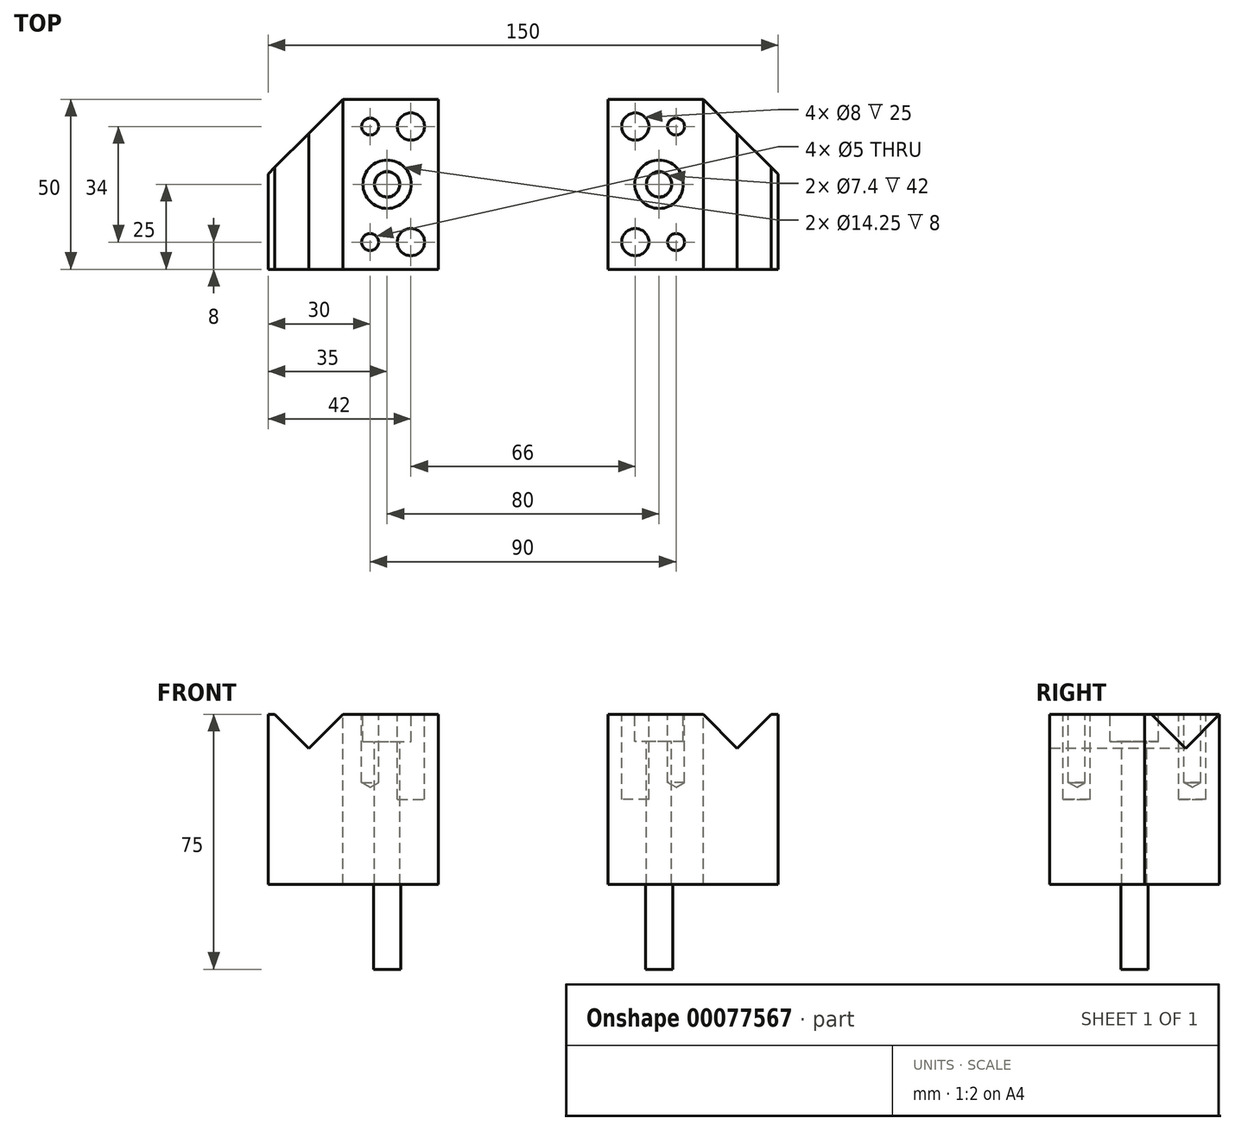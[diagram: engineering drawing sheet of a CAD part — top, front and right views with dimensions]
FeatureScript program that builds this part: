
annotation { "Feature Type Name" : "Feature", "Feature Type Description" : "" }
export const myFeature = defineFeature(function(context is Context, id is Id, definition is map)
    precondition{}
    {
        {
            var Q0;
            Q0=qCreatedBy(makeId("Top.planeOp"),FACE);
            var sketch = newSketch(context, id + "F0", { "sketchPlane" : qUnion([Q0])});
            skLineSegment(sketch, "E0.bottom", {"start": v(25, 25) * mm, "end": v(-25, 25) * mm});
            skLineSegment(sketch, "E0.top", {"start": v(25, -25) * mm, "end": v(-25, -25) * mm});
            skLineSegment(sketch, "E0.left", {"start": v(25, 25) * mm, "end": v(25, -25) * mm});
            skLineSegment(sketch, "E0.right", {"start": v(-25, 25) * mm, "end": v(-25, -25) * mm});
            skPoint(sketch, "E0.middle", {"position": v(0, 0) * mm});
            skSolve(sketch);
        }
        {
            var Q0;
            Q0 = qSketchRegion(id + "F0", true);
            var Q1;
            Q1 = qSketchRegion(id + "F2", true);
            extrude(context, id + "F1", {"entities" : qUnion([Q0, Q1]), "depth" : 50 * mm});
        }
        {
            var Q0;
            Q0=makeQuery(id+"F1.opExtrude","SWEPT_FACE",FACE,{"disambiguationData":[OSD([sQuery(id+"F0.wireOp",EDGE,"E0.top")])]});
            var sketch = newSketch(context, id + "F2", { "sketchPlane" : qUnion([Q0])});
            skLineSegment(sketch, "E1", {"start": v(23, 50) * mm, "end": v(13, 40) * mm});
            skLineSegment(sketch, "E2", {"start": v(13, 40) * mm, "end": v(3, 50) * mm});
            skLineSegment(sketch, "E3", {"start": v(3, 50) * mm, "end": v(23, 50) * mm});
            skSolve(sketch);
        }
        {
            var Q0;
            Q0=makeQuery(id+"F2.imprint","IMPRINT",FACE,{"disambiguationData":[TD([[makeQuery(id+"F2.imprint","IMPRINT",EDGE,{"derivedFrom":sQuery(id+"F2.wireOp",EDGE,"E1")}),-1.0]])]});
            extrude(context, id + "F3", {"entities" : qUnion([Q0]), "operationType" : NewBodyOperationType.REMOVE, "endBound" : BoundingType.THROUGH_ALL, "oppositeDirection" : true, "depth" : 25 * mm});
        }
        {
            var Q0;
            {var subQ0=sQuery(id+"F0.wireOp",EDGE,"E0.bottom");var subQ1=sQuery(id+"F0.wireOp",EDGE,"E0.top");var subQ2=sQuery(id+"F0.wireOp",EDGE,"E0.right");Q0=makeQuery(id+"F3.boolean.opBoolean","SPLIT",FACE,{"disambiguationData":[TD([makeQuery(id+"F1.opExtrude","SWEPT_FACE",FACE,{"disambiguationData":[OSD([subQ2])]})])],"derivedFrom":makeQuery(id+"F1.opExtrude","CAP_FACE",FACE,{"disambiguationData":[OSD([subQ0,subQ1,sQuery(id+"F0.wireOp",EDGE,"E0.left"),subQ2])],"isStart":false})});}
            var sketch = newSketch(context, id + "F4", { "sketchPlane" : qUnion([Q0])});
            skCircle(sketch, "E4", {"center": v(-17, 17) * mm, "radius": 4 * mm});
            skCircle(sketch, "E5", {"center": v(-17, -17) * mm, "radius": 4 * mm});
            skSolve(sketch);
        }
        {
            var Q0;
            Q0 = qSketchRegion(id + "F4", true);
            extrude(context, id + "F5", {"entities" : qUnion([Q0]), "operationType" : NewBodyOperationType.REMOVE, "oppositeDirection" : true, "depth" : 25 * mm});
        }
        {
            var Q0;
            {var subQ0=sQuery(id+"F0.wireOp",EDGE,"E0.bottom");var subQ1=sQuery(id+"F0.wireOp",EDGE,"E0.top");var subQ2=sQuery(id+"F0.wireOp",EDGE,"E0.right");Q0=makeQuery(id+"F3.boolean.opBoolean","SPLIT",FACE,{"disambiguationData":[TD([makeQuery(id+"F1.opExtrude","SWEPT_FACE",FACE,{"disambiguationData":[OSD([subQ2])]})])],"derivedFrom":makeQuery(id+"F1.opExtrude","CAP_FACE",FACE,{"disambiguationData":[OSD([subQ0,subQ1,sQuery(id+"F0.wireOp",EDGE,"E0.left"),subQ2])],"isStart":false})});}
            var sketch = newSketch(context, id + "F6", { "sketchPlane" : qUnion([Q0])});
            skPoint(sketch, "E6", {"position": v(-15, 0) * mm});
            skPoint(sketch, "E7", {"position": v(-5, -17) * mm});
            skPoint(sketch, "E8", {"position": v(-10, 0) * mm});
            skLineSegment(sketch, "E9", {"start": v(-17, 17) * mm, "end": v(-17, -17) * mm});
            skLineSegment(sketch, "E10", {"start": v(-5, -17) * mm, "end": v(-5, 17) * mm});
            skPoint(sketch, "E11", {"position": v(-5, 17) * mm});
            skSolve(sketch);
        }
        {
            var Q0;
            Q0=sQuery(id+"F6.wireOp",VERTEX,"E7");
            var Q1;
            Q1=sQuery(id+"F6.wireOp",VERTEX,"E11");
            var Q2;
            Q2=makeQuery(id+"F1.opExtrude","SWEPT_BODY",BODY,{"disambiguationData":[OSD([sQuery(id+"F0.wireOp",EDGE,"E0.bottom"),sQuery(id+"F0.wireOp",EDGE,"E0.top"),sQuery(id+"F0.wireOp",EDGE,"E0.left"),sQuery(id+"F0.wireOp",EDGE,"E0.right")])]});
            hole(context, id + "F7", {"style" : HoleStyle.SIMPLE, "endStyle" : HoleEndStyle.BLIND, "standardTappedOrClearance" : lookupTablePath({ "standard" : "ISO", "engagement" : "75%", "pitch" : "1 mm", "size" : "M6", "type" : "Tapped" }), "standardBlindInLast" : lookupTablePath({ "standard" : "ISO", "engagement" : "75%", "pitch" : "1 mm", "size" : "M6", "type" : "Tapped" }), "holeDiameter" : 5 * mm, "holeDepth" : 20 * mm, "startFromSketch" : true, "locations" : qUnion([Q0, Q1]), "scope" : qUnion([Q2]), "majorDiameter" : 6 * mm});
        }
        {
            var Q0;
            Q0=sQuery(id+"F6.wireOp",VERTEX,"E8");
            var Q1;
            Q1=makeQuery(id+"F1.opExtrude","SWEPT_BODY",BODY,{"disambiguationData":[OSD([sQuery(id+"F0.wireOp",EDGE,"E0.bottom"),sQuery(id+"F0.wireOp",EDGE,"E0.top"),sQuery(id+"F0.wireOp",EDGE,"E0.left"),sQuery(id+"F0.wireOp",EDGE,"E0.right")])]});
            hole(context, id + "F8", {"style" : HoleStyle.C_BORE, "endStyle" : HoleEndStyle.BLIND, "standardTappedOrClearance" : lookupTablePath({ "standard" : "ISO", "engagement" : "25%", "pitch" : "1 mm", "size" : "M8", "type" : "Tapped" }), "standardBlindInLast" : lookupTablePath({ "standard" : "ISO", "engagement" : "25%", "pitch" : "1 mm", "size" : "M8", "type" : "Tapped" }), "holeDiameter" : 7.4 * mm, "cBoreDiameter" : 14.25 * mm, "cBoreDepth" : 8 * mm, "holeDepth" : 60 * mm, "startFromSketch" : true, "locations" : qUnion([Q0]), "scope" : qUnion([Q1])});
        }
        {
            var Q0;
            Q0=makeQuery(id+"F1.opExtrude","CAP_FACE",FACE,{"disambiguationData":[OSD([sQuery(id+"F0.wireOp",EDGE,"E0.bottom"),sQuery(id+"F0.wireOp",EDGE,"E0.top"),sQuery(id+"F0.wireOp",EDGE,"E0.left"),sQuery(id+"F0.wireOp",EDGE,"E0.right")])],"isStart":true});
            var sketch = newSketch(context, id + "F9", { "sketchPlane" : qUnion([Q0])});
            skCircle(sketch, "E12", {"center": v(-10, 0) * mm, "radius": 4 * mm});
            skSolve(sketch);
        }
        {
            var Q0;
            Q0 = qSketchRegion(id + "F9", true);
            extrude(context, id + "F10", {"entities" : qUnion([Q0]), "operationType" : NewBodyOperationType.ADD, "depth" : 25 * mm});
        }
        {
            var Q0;
            {var subQ0=sQuery(id+"F0.wireOp",EDGE,"E0.bottom");var subQ1=sQuery(id+"F0.wireOp",EDGE,"E0.top");var subQ2=sQuery(id+"F0.wireOp",EDGE,"E0.right");Q0=makeQuery(id+"F3.boolean.opBoolean","SPLIT",FACE,{"disambiguationData":[TD([makeQuery(id+"F1.opExtrude","SWEPT_FACE",FACE,{"disambiguationData":[OSD([subQ2])]})])],"derivedFrom":makeQuery(id+"F1.opExtrude","CAP_FACE",FACE,{"disambiguationData":[OSD([subQ0,subQ1,sQuery(id+"F0.wireOp",EDGE,"E0.left"),subQ2])],"isStart":false})});}
            var sketch = newSketch(context, id + "F11", { "sketchPlane" : qUnion([Q0])});
            skLineSegment(sketch, "E13", {"start": v(3, 25) * mm, "end": v(28, 0) * mm});
            skLineSegment(sketch, "E14", {"start": v(28, 0) * mm, "end": v(28, 25) * mm});
            skLineSegment(sketch, "E15", {"start": v(28, 25) * mm, "end": v(3, 25) * mm});
            skSolve(sketch);
        }
        {
            var Q0;
            Q0 = qSketchRegion(id + "F11", true);
            extrude(context, id + "F12", {"entities" : qUnion([Q0]), "operationType" : NewBodyOperationType.REMOVE, "endBound" : BoundingType.THROUGH_ALL, "oppositeDirection" : true, "depth" : 25 * mm});
        }
        {
            var Q0;
            Q0=makeQuery(id+"F1.opExtrude","SWEPT_BODY",BODY,{"disambiguationData":[OSD([sQuery(id+"F0.wireOp",EDGE,"E0.bottom"),sQuery(id+"F0.wireOp",EDGE,"E0.top"),sQuery(id+"F0.wireOp",EDGE,"E0.left"),sQuery(id+"F0.wireOp",EDGE,"E0.right")])]});
            var Q1;
            Q1=makeQuery(id+"F1.opExtrude","SWEPT_FACE",FACE,{"disambiguationData":[OSD([sQuery(id+"F0.wireOp",EDGE,"E0.right")])]});
            mirror(context, id + "F13", {"entities" : qUnion([Q0]), "mirrorPlane" : qUnion([Q1])});
        }
        {
            var Q0;
            Q0=makeQuery(id+"F13.opPattern","COPY",BODY,{"derivedFrom":makeQuery(id+"F1.opExtrude","SWEPT_BODY",BODY,{"disambiguationData":[OSD([sQuery(id+"F0.wireOp",EDGE,"E0.bottom"),sQuery(id+"F0.wireOp",EDGE,"E0.top"),sQuery(id+"F0.wireOp",EDGE,"E0.left"),sQuery(id+"F0.wireOp",EDGE,"E0.right")])]}),"instanceName":"1"});
            transform(context, id + "F14", {"entities" : qUnion([Q0]), "transformType" : TransformType.TRANSLATION_3D, "dx" : -50 * mm, "dy" : 0 * mm, "dz" : 0 * mm, "makeCopy" : false});
        }
    });
